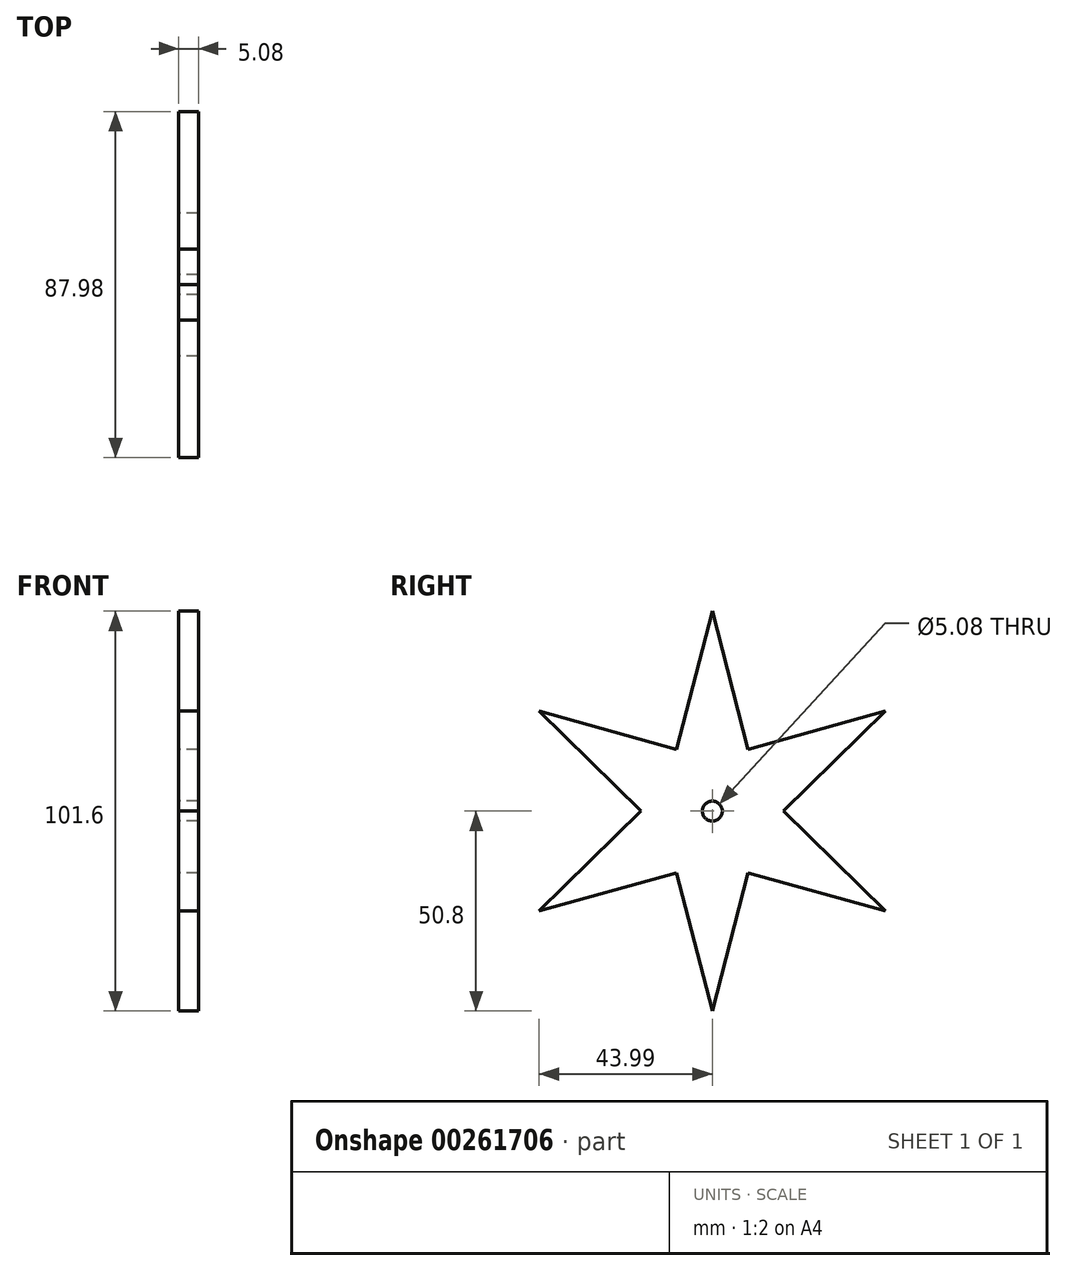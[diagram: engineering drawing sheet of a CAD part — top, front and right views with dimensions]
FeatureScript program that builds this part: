
annotation { "Feature Type Name" : "Feature", "Feature Type Description" : "" }
export const myFeature = defineFeature(function(context is Context, id is Id, definition is map)
    precondition{}
    {
        {
            var Q0;
            Q0=qCreatedBy(makeId("Right.planeOp"),FACE);
            var sketch = newSketch(context, id + "F0", { "sketchPlane" : qUnion([Q0])});
            skCircle(sketch, "E0", {"center": v(0, 0) * mm, "radius": 2.54 * mm});
            skCircle(sketch, "E1", {"center": v(0, 0) * mm, "radius": 12.7 * mm});
            skCircle(sketch, "E2", {"center": v(0, 0) * mm, "radius": 50.8 * mm});
            skLineSegment(sketch, "E3", {"start": v(0, 0) * mm, "end": v(0, 50.8) * mm});
            skLineSegment(sketch, "E4", {"start": v(0, 0) * mm, "end": v(44, -25.4) * mm});
            skLineSegment(sketch, "E5", {"start": v(0, 0) * mm, "end": v(-44, -25.4) * mm});
            skLineSegment(sketch, "E6", {"start": v(0, 50.8) * mm, "end": v(12.3, 3.18) * mm});
            skLineSegment(sketch, "E7", {"start": v(44, -25.4) * mm, "end": v(8.9, 9.06) * mm});
            skLineSegment(sketch, "E8", {"start": v(-44, -25.4) * mm, "end": v(3.4, -12.24) * mm});
            skLineSegment(sketch, "E9", {"start": v(44, -25.4) * mm, "end": v(-3.4, -12.24) * mm});
            skLineSegment(sketch, "E10", {"start": v(-44, -25.4) * mm, "end": v(-8.9, 9.06) * mm});
            skLineSegment(sketch, "E11", {"start": v(-12.3, 3.18) * mm, "end": v(0, 50.8) * mm});
            skLineSegment(sketch, "E12", {"start": v(0, 0) * mm, "end": v(44, 25.4) * mm});
            skLineSegment(sketch, "E13", {"start": v(0, 0) * mm, "end": v(0, -50.8) * mm});
            skLineSegment(sketch, "E14", {"start": v(0, 0) * mm, "end": v(-44, 25.4) * mm});
            skLineSegment(sketch, "E15", {"start": v(-44, 25.4) * mm, "end": v(-8.9, -9.06) * mm});
            skLineSegment(sketch, "E16", {"start": v(-44, 25.4) * mm, "end": v(3.4, 12.24) * mm});
            skLineSegment(sketch, "E17", {"start": v(44, 25.4) * mm, "end": v(-3.4, 12.24) * mm});
            skLineSegment(sketch, "E18", {"start": v(44, 25.4) * mm, "end": v(8.9, -9.06) * mm});
            skLineSegment(sketch, "E19", {"start": v(0, -50.8) * mm, "end": v(-12.3, -3.18) * mm});
            skLineSegment(sketch, "E20", {"start": v(0, -50.8) * mm, "end": v(12.3, -3.18) * mm});
            skSolve(sketch);
        }
        {
            var Q0;
            {var subQ0=sQuery(id+"F0.wireOp",EDGE,"E9");var subQ1=sQuery(id+"F0.wireOp",EDGE,"E1");var subQ2=makeQuery(id+"F0.imprint","INTERSECT",VERTEX,{"derivedFrom":[subQ1,subQ0]});Q0=makeQuery(id+"F0.imprint","IMPRINT",FACE,{"disambiguationData":[TD([[makeQuery(id+"F0.imprint","IMPRINT",EDGE,{"disambiguationData":[TD([[subQ2,1.0]])],"derivedFrom":subQ1}),-1.0]])]});}
            var Q1;
            {var subQ0=sQuery(id+"F0.wireOp",EDGE,"E10");var subQ1=sQuery(id+"F0.wireOp",EDGE,"E1");var subQ2=makeQuery(id+"F0.imprint","INTERSECT",VERTEX,{"derivedFrom":[subQ1,subQ0]});Q1=makeQuery(id+"F0.imprint","IMPRINT",FACE,{"disambiguationData":[TD([[makeQuery(id+"F0.imprint","IMPRINT",EDGE,{"disambiguationData":[TD([[subQ2,1.0]])],"derivedFrom":subQ1}),-1.0]])]});}
            var Q2;
            {var subQ2=sQuery(id+"F0.wireOp",EDGE,"E5");var subQ7=sQuery(id+"F0.wireOp",EDGE,"E0");var subQ9=makeQuery(id+"F0.imprint","INTERSECT",VERTEX,{"derivedFrom":[subQ7,subQ2]});Q2=makeQuery(id+"F0.imprint","IMPRINT",FACE,{"disambiguationData":[TD([[makeQuery(id+"F0.imprint","IMPRINT",EDGE,{"disambiguationData":[TD([[subQ9,1.0]])],"derivedFrom":subQ7}),-1.0]])]});}
            var Q3;
            {var subQ5=sQuery(id+"F0.wireOp",EDGE,"E5");var subQ7=sQuery(id+"F0.wireOp",EDGE,"E0");var subQ9=makeQuery(id+"F0.imprint","INTERSECT",VERTEX,{"derivedFrom":[subQ7,subQ5]});Q3=makeQuery(id+"F0.imprint","IMPRINT",FACE,{"disambiguationData":[TD([[makeQuery(id+"F0.imprint","IMPRINT",EDGE,{"disambiguationData":[TD([[subQ9,-1.0]])],"derivedFrom":subQ7}),-1.0]])]});}
            var Q4;
            {var subQ5=sQuery(id+"F0.wireOp",EDGE,"E3");var subQ7=sQuery(id+"F0.wireOp",EDGE,"E0");var subQ8=makeQuery(id+"F0.imprint","INTERSECT",VERTEX,{"derivedFrom":[subQ7,subQ5]});Q4=makeQuery(id+"F0.imprint","IMPRINT",FACE,{"disambiguationData":[TD([[makeQuery(id+"F0.imprint","IMPRINT",EDGE,{"disambiguationData":[TD([[subQ8,1.0]])],"derivedFrom":subQ7}),-1.0]])]});}
            var Q5;
            {var subQ0=sQuery(id+"F0.wireOp",EDGE,"E8");var subQ1=sQuery(id+"F0.wireOp",EDGE,"E1");var subQ2=makeQuery(id+"F0.imprint","INTERSECT",VERTEX,{"derivedFrom":[subQ1,subQ0]});Q5=makeQuery(id+"F0.imprint","IMPRINT",FACE,{"disambiguationData":[TD([[makeQuery(id+"F0.imprint","IMPRINT",EDGE,{"disambiguationData":[TD([[subQ2,-1.0]])],"derivedFrom":subQ1}),-1.0]])]});}
            var Q6;
            {var subQ0=sQuery(id+"F0.wireOp",EDGE,"E6");var subQ1=sQuery(id+"F0.wireOp",EDGE,"E1");var subQ2=makeQuery(id+"F0.imprint","INTERSECT",VERTEX,{"derivedFrom":[subQ1,subQ0]});Q6=makeQuery(id+"F0.imprint","IMPRINT",FACE,{"disambiguationData":[TD([[makeQuery(id+"F0.imprint","IMPRINT",EDGE,{"disambiguationData":[TD([[subQ2,1.0]])],"derivedFrom":subQ1}),-1.0]])]});}
            var Q7;
            {var subQ0=sQuery(id+"F0.wireOp",EDGE,"E7");var subQ1=sQuery(id+"F0.wireOp",EDGE,"E1");var subQ2=makeQuery(id+"F0.imprint","INTERSECT",VERTEX,{"derivedFrom":[subQ1,subQ0]});Q7=makeQuery(id+"F0.imprint","IMPRINT",FACE,{"disambiguationData":[TD([[makeQuery(id+"F0.imprint","IMPRINT",EDGE,{"disambiguationData":[TD([[subQ2,-1.0]])],"derivedFrom":subQ1}),-1.0]])]});}
            var Q8;
            {var subQ0=sQuery(id+"F0.wireOp",EDGE,"E11");var subQ1=sQuery(id+"F0.wireOp",EDGE,"E1");var subQ2=makeQuery(id+"F0.imprint","INTERSECT",VERTEX,{"derivedFrom":[subQ1,subQ0]});Q8=makeQuery(id+"F0.imprint","IMPRINT",FACE,{"disambiguationData":[TD([[makeQuery(id+"F0.imprint","IMPRINT",EDGE,{"disambiguationData":[TD([[subQ2,-1.0]])],"derivedFrom":subQ1}),-1.0]])]});}
            var Q9;
            {var subQ0=sQuery(id+"F0.wireOp",EDGE,"E10");var subQ1=sQuery(id+"F0.wireOp",EDGE,"E1");var subQ2=makeQuery(id+"F0.imprint","INTERSECT",VERTEX,{"derivedFrom":[subQ1,subQ0]});Q9=makeQuery(id+"F0.imprint","IMPRINT",FACE,{"disambiguationData":[TD([[makeQuery(id+"F0.imprint","IMPRINT",EDGE,{"disambiguationData":[TD([[subQ2,-1.0]])],"derivedFrom":subQ1}),-1.0]])]});}
            var Q10;
            {var subQ0=sQuery(id+"F0.wireOp",EDGE,"E6");var subQ1=sQuery(id+"F0.wireOp",EDGE,"E1");var subQ2=makeQuery(id+"F0.imprint","INTERSECT",VERTEX,{"derivedFrom":[subQ1,subQ0]});Q10=makeQuery(id+"F0.imprint","IMPRINT",FACE,{"disambiguationData":[TD([[makeQuery(id+"F0.imprint","IMPRINT",EDGE,{"disambiguationData":[TD([[subQ2,-1.0]])],"derivedFrom":subQ1}),-1.0]])]});}
            var Q11;
            {var subQ0=sQuery(id+"F0.wireOp",EDGE,"E8");var subQ1=sQuery(id+"F0.wireOp",EDGE,"E1");var subQ2=makeQuery(id+"F0.imprint","INTERSECT",VERTEX,{"derivedFrom":[subQ1,subQ0]});Q11=makeQuery(id+"F0.imprint","IMPRINT",FACE,{"disambiguationData":[TD([[makeQuery(id+"F0.imprint","IMPRINT",EDGE,{"disambiguationData":[TD([[subQ2,1.0]])],"derivedFrom":subQ1}),-1.0]])]});}
            var Q12;
            {var subQ4=sQuery(id+"F0.wireOp",EDGE,"E3");var subQ5=sQuery(id+"F0.wireOp",EDGE,"E0");var subQ6=makeQuery(id+"F0.imprint","INTERSECT",VERTEX,{"derivedFrom":[subQ5,subQ4]});Q12=makeQuery(id+"F0.imprint","IMPRINT",FACE,{"disambiguationData":[TD([[makeQuery(id+"F0.imprint","IMPRINT",EDGE,{"disambiguationData":[TD([[subQ6,-1.0]])],"derivedFrom":subQ5}),-1.0]])]});}
            var Q13;
            {var subQ5=sQuery(id+"F0.wireOp",EDGE,"E12");var subQ7=sQuery(id+"F0.wireOp",EDGE,"E0");var subQ8=makeQuery(id+"F0.imprint","INTERSECT",VERTEX,{"derivedFrom":[subQ7,subQ5]});Q13=makeQuery(id+"F0.imprint","IMPRINT",FACE,{"disambiguationData":[TD([[makeQuery(id+"F0.imprint","IMPRINT",EDGE,{"disambiguationData":[TD([[subQ8,1.0]])],"derivedFrom":subQ7}),-1.0]])]});}
            var Q14;
            {var subQ4=sQuery(id+"F0.wireOp",EDGE,"E13");var subQ5=sQuery(id+"F0.wireOp",EDGE,"E0");var subQ6=makeQuery(id+"F0.imprint","INTERSECT",VERTEX,{"derivedFrom":[subQ5,subQ4]});Q14=makeQuery(id+"F0.imprint","IMPRINT",FACE,{"disambiguationData":[TD([[makeQuery(id+"F0.imprint","IMPRINT",EDGE,{"disambiguationData":[TD([[subQ6,-1.0]])],"derivedFrom":subQ5}),-1.0]])]});}
            var Q15;
            {var subQ0=sQuery(id+"F0.wireOp",EDGE,"E20");var subQ1=sQuery(id+"F0.wireOp",EDGE,"E9");var subQ2=makeQuery(id+"F0.imprint","INTERSECT",VERTEX,{"derivedFrom":[subQ1,subQ0]});Q15=makeQuery(id+"F0.imprint","IMPRINT",FACE,{"disambiguationData":[TD([[makeQuery(id+"F0.imprint","IMPRINT",EDGE,{"disambiguationData":[TD([[subQ2,-1.0]])],"derivedFrom":subQ1}),1.0]])]});}
            var Q16;
            {var subQ0=sQuery(id+"F0.wireOp",EDGE,"E19");var subQ1=sQuery(id+"F0.wireOp",EDGE,"E8");var subQ2=makeQuery(id+"F0.imprint","INTERSECT",VERTEX,{"derivedFrom":[subQ1,subQ0]});Q16=makeQuery(id+"F0.imprint","IMPRINT",FACE,{"disambiguationData":[TD([[makeQuery(id+"F0.imprint","IMPRINT",EDGE,{"disambiguationData":[TD([[subQ2,-1.0]])],"derivedFrom":subQ1}),-1.0]])]});}
            var Q17;
            {var subQ0=sQuery(id+"F0.wireOp",EDGE,"E8");var subQ3=sQuery(id+"F0.wireOp",EDGE,"E19");var subQ5=makeQuery(id+"F0.imprint","INTERSECT",VERTEX,{"derivedFrom":[subQ0,subQ3]});Q17=makeQuery(id+"F0.imprint","IMPRINT",FACE,{"disambiguationData":[TD([[makeQuery(id+"F0.imprint","IMPRINT",EDGE,{"disambiguationData":[TD([[subQ5,-1.0]])],"derivedFrom":subQ3}),1.0]])]});}
            var Q18;
            {var subQ0=sQuery(id+"F0.wireOp",EDGE,"E10");var subQ3=sQuery(id+"F0.wireOp",EDGE,"E15");var subQ5=makeQuery(id+"F0.imprint","INTERSECT",VERTEX,{"derivedFrom":[subQ0,subQ3]});Q18=makeQuery(id+"F0.imprint","IMPRINT",FACE,{"disambiguationData":[TD([[makeQuery(id+"F0.imprint","IMPRINT",EDGE,{"disambiguationData":[TD([[subQ5,-1.0]])],"derivedFrom":subQ3}),-1.0]])]});}
            var Q19;
            {var subQ0=sQuery(id+"F0.wireOp",EDGE,"E16");var subQ1=sQuery(id+"F0.wireOp",EDGE,"E11");var subQ2=makeQuery(id+"F0.imprint","INTERSECT",VERTEX,{"derivedFrom":[subQ1,subQ0]});Q19=makeQuery(id+"F0.imprint","IMPRINT",FACE,{"disambiguationData":[TD([[makeQuery(id+"F0.imprint","IMPRINT",EDGE,{"disambiguationData":[TD([[subQ2,1.0]])],"derivedFrom":subQ1}),1.0]])]});}
            var Q20;
            {var subQ0=sQuery(id+"F0.wireOp",EDGE,"E11");var subQ3=sQuery(id+"F0.wireOp",EDGE,"E16");var subQ5=makeQuery(id+"F0.imprint","INTERSECT",VERTEX,{"derivedFrom":[subQ0,subQ3]});Q20=makeQuery(id+"F0.imprint","IMPRINT",FACE,{"disambiguationData":[TD([[makeQuery(id+"F0.imprint","IMPRINT",EDGE,{"disambiguationData":[TD([[subQ5,-1.0]])],"derivedFrom":subQ3}),1.0]])]});}
            var Q21;
            {var subQ0=sQuery(id+"F0.wireOp",EDGE,"E6");var subQ3=sQuery(id+"F0.wireOp",EDGE,"E17");var subQ5=makeQuery(id+"F0.imprint","INTERSECT",VERTEX,{"derivedFrom":[subQ0,subQ3]});Q21=makeQuery(id+"F0.imprint","IMPRINT",FACE,{"disambiguationData":[TD([[makeQuery(id+"F0.imprint","IMPRINT",EDGE,{"disambiguationData":[TD([[subQ5,-1.0]])],"derivedFrom":subQ3}),-1.0]])]});}
            var Q22;
            {var subQ0=sQuery(id+"F0.wireOp",EDGE,"E17");var subQ1=sQuery(id+"F0.wireOp",EDGE,"E6");var subQ2=makeQuery(id+"F0.imprint","INTERSECT",VERTEX,{"derivedFrom":[subQ1,subQ0]});Q22=makeQuery(id+"F0.imprint","IMPRINT",FACE,{"disambiguationData":[TD([[makeQuery(id+"F0.imprint","IMPRINT",EDGE,{"disambiguationData":[TD([[subQ2,-1.0]])],"derivedFrom":subQ1}),1.0]])]});}
            var Q23;
            {var subQ0=sQuery(id+"F0.wireOp",EDGE,"E18");var subQ1=sQuery(id+"F0.wireOp",EDGE,"E7");var subQ2=makeQuery(id+"F0.imprint","INTERSECT",VERTEX,{"derivedFrom":[subQ1,subQ0]});Q23=makeQuery(id+"F0.imprint","IMPRINT",FACE,{"disambiguationData":[TD([[makeQuery(id+"F0.imprint","IMPRINT",EDGE,{"disambiguationData":[TD([[subQ2,-1.0]])],"derivedFrom":subQ1}),-1.0]])]});}
            var Q24;
            {var subQ0=sQuery(id+"F0.wireOp",EDGE,"E9");var subQ3=sQuery(id+"F0.wireOp",EDGE,"E20");var subQ5=makeQuery(id+"F0.imprint","INTERSECT",VERTEX,{"derivedFrom":[subQ0,subQ3]});Q24=makeQuery(id+"F0.imprint","IMPRINT",FACE,{"disambiguationData":[TD([[makeQuery(id+"F0.imprint","IMPRINT",EDGE,{"disambiguationData":[TD([[subQ5,-1.0]])],"derivedFrom":subQ3}),-1.0]])]});}
            var Q25;
            {var subQ0=sQuery(id+"F0.wireOp",EDGE,"E7");var subQ3=sQuery(id+"F0.wireOp",EDGE,"E18");var subQ5=makeQuery(id+"F0.imprint","INTERSECT",VERTEX,{"derivedFrom":[subQ0,subQ3]});Q25=makeQuery(id+"F0.imprint","IMPRINT",FACE,{"disambiguationData":[TD([[makeQuery(id+"F0.imprint","IMPRINT",EDGE,{"disambiguationData":[TD([[subQ5,-1.0]])],"derivedFrom":subQ3}),1.0]])]});}
            var Q26;
            {var subQ0=sQuery(id+"F0.wireOp",EDGE,"E15");var subQ1=sQuery(id+"F0.wireOp",EDGE,"E10");var subQ2=makeQuery(id+"F0.imprint","INTERSECT",VERTEX,{"derivedFrom":[subQ1,subQ0]});Q26=makeQuery(id+"F0.imprint","IMPRINT",FACE,{"disambiguationData":[TD([[makeQuery(id+"F0.imprint","IMPRINT",EDGE,{"disambiguationData":[TD([[subQ2,-1.0]])],"derivedFrom":subQ1}),1.0]])]});}
            var Q27;
            {var subQ0=sQuery(id+"F0.wireOp",EDGE,"E15");var subQ1=sQuery(id+"F0.wireOp",EDGE,"E1");var subQ2=makeQuery(id+"F0.imprint","INTERSECT",VERTEX,{"derivedFrom":[subQ1,subQ0]});Q27=makeQuery(id+"F0.imprint","IMPRINT",FACE,{"disambiguationData":[TD([[makeQuery(id+"F0.imprint","IMPRINT",EDGE,{"disambiguationData":[TD([[subQ2,1.0]])],"derivedFrom":subQ1}),-1.0]])]});}
            var Q28;
            {var subQ0=sQuery(id+"F0.wireOp",EDGE,"E19");var subQ1=sQuery(id+"F0.wireOp",EDGE,"E1");var subQ2=makeQuery(id+"F0.imprint","INTERSECT",VERTEX,{"derivedFrom":[subQ1,subQ0]});Q28=makeQuery(id+"F0.imprint","IMPRINT",FACE,{"disambiguationData":[TD([[makeQuery(id+"F0.imprint","IMPRINT",EDGE,{"disambiguationData":[TD([[subQ2,-1.0]])],"derivedFrom":subQ1}),-1.0]])]});}
            var Q29;
            {var subQ0=sQuery(id+"F0.wireOp",EDGE,"E9");var subQ1=sQuery(id+"F0.wireOp",EDGE,"E1");var subQ2=makeQuery(id+"F0.imprint","INTERSECT",VERTEX,{"derivedFrom":[subQ1,subQ0]});Q29=makeQuery(id+"F0.imprint","IMPRINT",FACE,{"disambiguationData":[TD([[makeQuery(id+"F0.imprint","IMPRINT",EDGE,{"disambiguationData":[TD([[subQ2,-1.0]])],"derivedFrom":subQ1}),-1.0]])]});}
            var Q30;
            {var subQ0=sQuery(id+"F0.wireOp",EDGE,"E18");var subQ1=sQuery(id+"F0.wireOp",EDGE,"E1");var subQ2=makeQuery(id+"F0.imprint","INTERSECT",VERTEX,{"derivedFrom":[subQ1,subQ0]});Q30=makeQuery(id+"F0.imprint","IMPRINT",FACE,{"disambiguationData":[TD([[makeQuery(id+"F0.imprint","IMPRINT",EDGE,{"disambiguationData":[TD([[subQ2,-1.0]])],"derivedFrom":subQ1}),-1.0]])]});}
            var Q31;
            {var subQ0=sQuery(id+"F0.wireOp",EDGE,"E20");var subQ1=sQuery(id+"F0.wireOp",EDGE,"E1");var subQ2=makeQuery(id+"F0.imprint","INTERSECT",VERTEX,{"derivedFrom":[subQ1,subQ0]});Q31=makeQuery(id+"F0.imprint","IMPRINT",FACE,{"disambiguationData":[TD([[makeQuery(id+"F0.imprint","IMPRINT",EDGE,{"disambiguationData":[TD([[subQ2,1.0]])],"derivedFrom":subQ1}),-1.0]])]});}
            var Q32;
            {var subQ0=sQuery(id+"F0.wireOp",EDGE,"E11");var subQ1=sQuery(id+"F0.wireOp",EDGE,"E1");var subQ2=makeQuery(id+"F0.imprint","INTERSECT",VERTEX,{"derivedFrom":[subQ1,subQ0]});Q32=makeQuery(id+"F0.imprint","IMPRINT",FACE,{"disambiguationData":[TD([[makeQuery(id+"F0.imprint","IMPRINT",EDGE,{"disambiguationData":[TD([[subQ2,1.0]])],"derivedFrom":subQ1}),-1.0]])]});}
            var Q33;
            {var subQ0=sQuery(id+"F0.wireOp",EDGE,"E17");var subQ1=sQuery(id+"F0.wireOp",EDGE,"E1");var subQ2=makeQuery(id+"F0.imprint","INTERSECT",VERTEX,{"derivedFrom":[subQ1,subQ0]});Q33=makeQuery(id+"F0.imprint","IMPRINT",FACE,{"disambiguationData":[TD([[makeQuery(id+"F0.imprint","IMPRINT",EDGE,{"disambiguationData":[TD([[subQ2,1.0]])],"derivedFrom":subQ1}),-1.0]])]});}
            var Q34;
            {var subQ0=sQuery(id+"F0.wireOp",EDGE,"E16");var subQ1=sQuery(id+"F0.wireOp",EDGE,"E1");var subQ2=makeQuery(id+"F0.imprint","INTERSECT",VERTEX,{"derivedFrom":[subQ1,subQ0]});Q34=makeQuery(id+"F0.imprint","IMPRINT",FACE,{"disambiguationData":[TD([[makeQuery(id+"F0.imprint","IMPRINT",EDGE,{"disambiguationData":[TD([[subQ2,-1.0]])],"derivedFrom":subQ1}),-1.0]])]});}
            var Q35;
            {var subQ0=sQuery(id+"F0.wireOp",EDGE,"E7");var subQ1=sQuery(id+"F0.wireOp",EDGE,"E1");var subQ2=makeQuery(id+"F0.imprint","INTERSECT",VERTEX,{"derivedFrom":[subQ1,subQ0]});Q35=makeQuery(id+"F0.imprint","IMPRINT",FACE,{"disambiguationData":[TD([[makeQuery(id+"F0.imprint","IMPRINT",EDGE,{"disambiguationData":[TD([[subQ2,1.0]])],"derivedFrom":subQ1}),-1.0]])]});}
            extrude(context, id + "F1", {"entities" : qUnion([Q0, Q1, Q2, Q3, Q4, Q5, Q6, Q7, Q8, Q9, Q10, Q11, Q12, Q13, Q14, Q15, Q16, Q17, Q18, Q19, Q20, Q21, Q22, Q23, Q24, Q25, Q26, Q27, Q28, Q29, Q30, Q31, Q32, Q33, Q34, Q35]), "depth" : 5.08 * mm});
        }
    });
